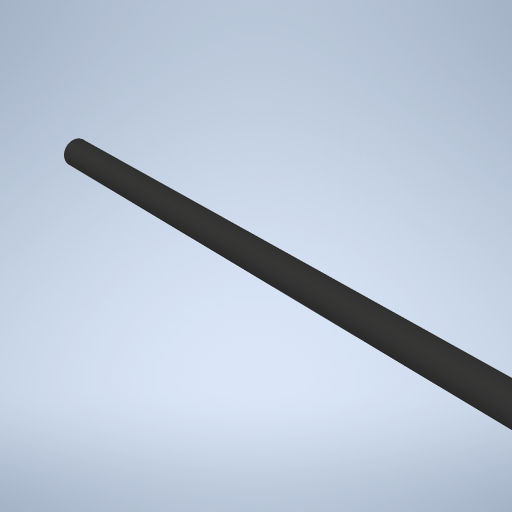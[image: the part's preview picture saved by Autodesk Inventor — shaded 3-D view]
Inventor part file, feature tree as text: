
AUTODESK INVENTOR PART (.ipt)
format: ipt  version: 2023.4 (Build 274418000, 418)  size: 237,568 bytes
history: native  units: in
note: dims shown in document units (in); Inventor stores cm internally (conversion verified against a paired STEP export)
features: extrude x1, sketch x1
ambient origin geometry x8: Origin, YZ Plane, XZ Plane, XY Plane, X Axis, Y Axis, Z Axis, Center Point
bodies: Solid1 (feature_tree)
feature tree (2):
  extrude  "Extrusion1"  Depth=26.375in TaperAngle=0.0deg
  sketch  "Sketch1"  dims[d0=1.25in d2=26.375in d3=0.0in d4=0.125in]
